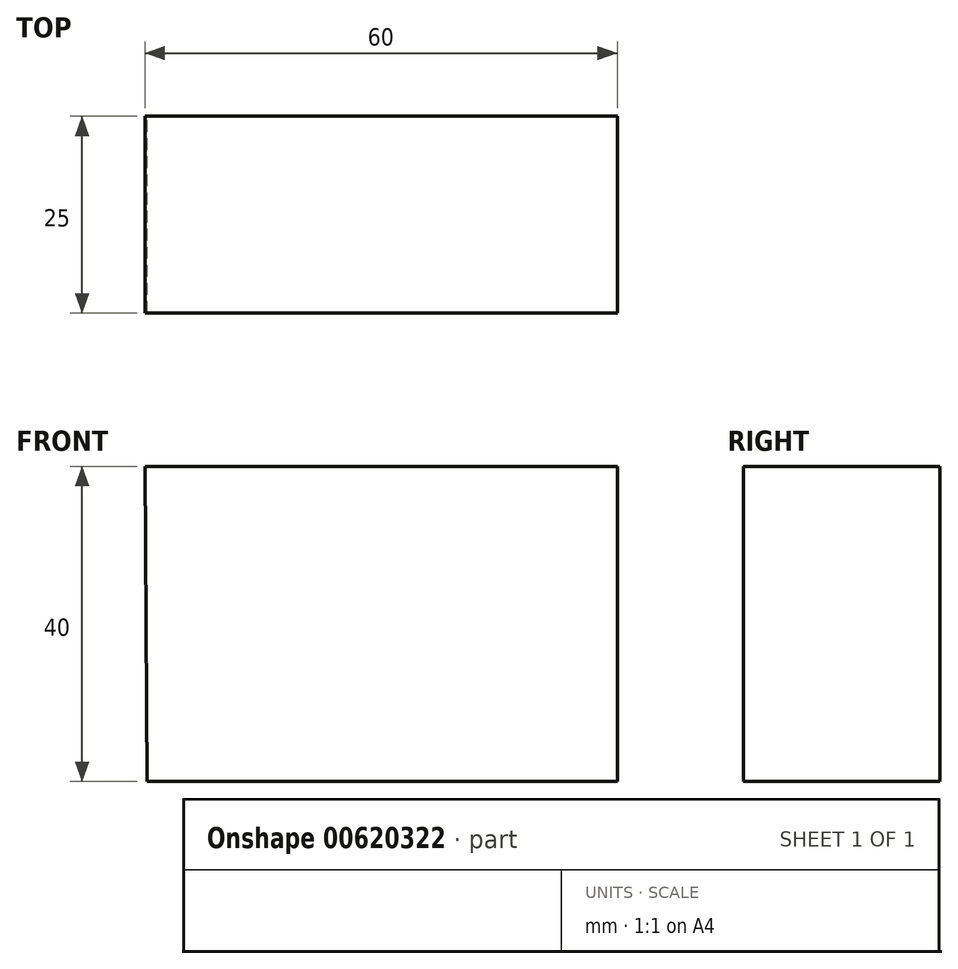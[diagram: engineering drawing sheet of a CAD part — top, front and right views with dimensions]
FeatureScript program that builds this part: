
annotation { "Feature Type Name" : "Feature", "Feature Type Description" : "" }
export const myFeature = defineFeature(function(context is Context, id is Id, definition is map)
    precondition{}
    {
        {
            var Q0;
            Q0=qCreatedBy(makeId("Front.planeOp"),FACE);
            var sketch = newSketch(context, id + "F0", { "sketchPlane" : qUnion([Q0])});
            skLineSegment(sketch, "E0", {"start": v(-70.2, 38.37) * mm, "end": v(-10.2, 38.37) * mm});
            skLineSegment(sketch, "E1", {"start": v(-10.2, 38.37) * mm, "end": v(-10.2, -1.63) * mm});
            skLineSegment(sketch, "E2", {"start": v(-10.2, -1.63) * mm, "end": v(-69.91, -1.63) * mm});
            skLineSegment(sketch, "E3", {"start": v(-69.91, -1.63) * mm, "end": v(-70.2, 38.37) * mm});
            skSolve(sketch);
        }
        {
            var Q0;
            Q0 = qSketchRegion(id + "F0", true);
            extrude(context, id + "F1", {"entities" : qUnion([Q0]), "depth" : 25 * mm, "offsetDistance" : 25 * mm});
        }
    });
